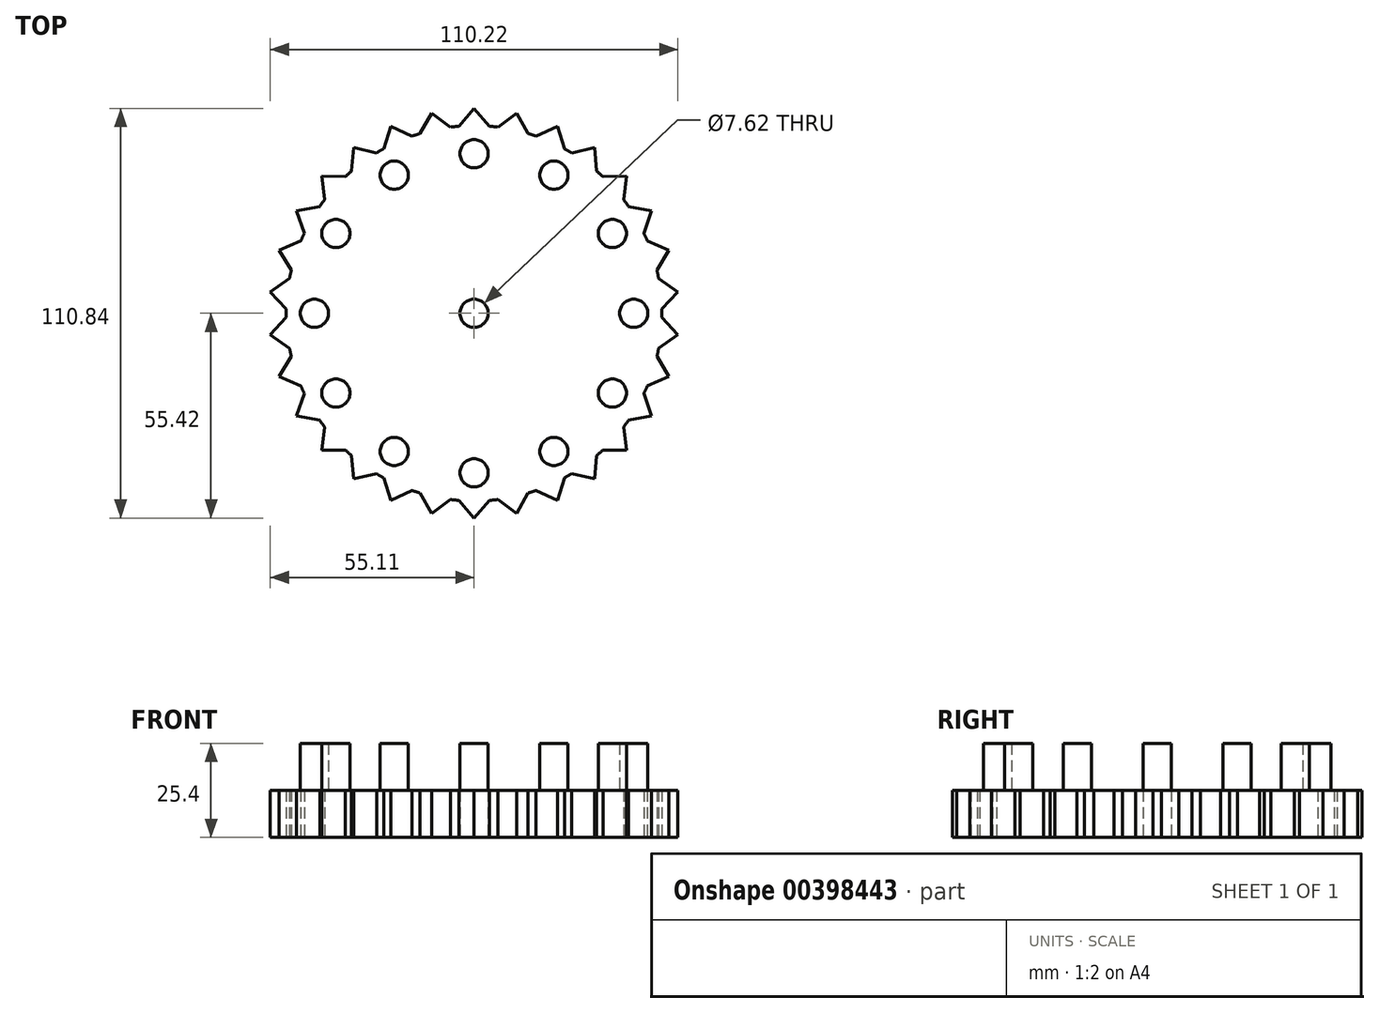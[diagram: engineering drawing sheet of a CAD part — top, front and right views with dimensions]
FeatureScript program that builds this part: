
annotation { "Feature Type Name" : "Feature", "Feature Type Description" : "" }
export const myFeature = defineFeature(function(context is Context, id is Id, definition is map)
    precondition{}
    {
        {
            var Q0;
            Q0=qCreatedBy(makeId("Top.planeOp"),FACE);
            var sketch = newSketch(context, id + "F0", { "sketchPlane" : qUnion([Q0])});
            skCircle(sketch, "E0", {"center": v(0, 0) * mm, "radius": 50.8 * mm});
            skCircle(sketch, "E1", {"center": v(0, 0) * mm, "radius": 3.81 * mm});
            skLineSegment(sketch, "E2", {"start": v(-4.17, 50.63) * mm, "end": v(0, 55.42) * mm});
            skLineSegment(sketch, "E3", {"start": v(0, 55.42) * mm, "end": v(4.17, 50.63) * mm});
            skLineSegment(sketch, "E4.1.0", {"start": v(-11.52, 54.2) * mm, "end": v(-6.45, 50.39) * mm});
            skLineSegment(sketch, "E4.1.1", {"start": v(-14.6, 48.65) * mm, "end": v(-11.52, 54.2) * mm});
            skLineSegment(sketch, "E4.2.0", {"start": v(-22.54, 50.62) * mm, "end": v(-16.78, 47.95) * mm});
            skLineSegment(sketch, "E4.2.1", {"start": v(-24.4, 44.55) * mm, "end": v(-22.54, 50.62) * mm});
            skLineSegment(sketch, "E4.3.0", {"start": v(-32.57, 44.83) * mm, "end": v(-26.38, 43.41) * mm});
            skLineSegment(sketch, "E4.3.1", {"start": v(-33.13, 38.5) * mm, "end": v(-32.57, 44.83) * mm});
            skLineSegment(sketch, "E4.4.0", {"start": v(-41.18, 37.08) * mm, "end": v(-34.83, 36.98) * mm});
            skLineSegment(sketch, "E4.4.1", {"start": v(-40.42, 30.78) * mm, "end": v(-41.18, 37.08) * mm});
            skLineSegment(sketch, "E4.5.0", {"start": v(-48, 27.7) * mm, "end": v(-41.76, 28.93) * mm});
            skLineSegment(sketch, "E4.5.1", {"start": v(-45.93, 21.7) * mm, "end": v(-48, 27.7) * mm});
            skLineSegment(sketch, "E4.6.0", {"start": v(-52.7, 17.12) * mm, "end": v(-46.86, 19.61) * mm});
            skLineSegment(sketch, "E4.6.1", {"start": v(-49.44, 11.68) * mm, "end": v(-52.7, 17.12) * mm});
            skLineSegment(sketch, "E4.7.0", {"start": v(-55.11, 5.8) * mm, "end": v(-49.91, 9.44) * mm});
            skLineSegment(sketch, "E4.7.1", {"start": v(-50.79, 1.14) * mm, "end": v(-55.11, 5.8) * mm});
            skLineSegment(sketch, "E4.8.0", {"start": v(-55.11, -5.8) * mm, "end": v(-50.79, -1.14) * mm});
            skLineSegment(sketch, "E4.8.1", {"start": v(-49.91, -9.44) * mm, "end": v(-55.11, -5.8) * mm});
            skLineSegment(sketch, "E4.9.0", {"start": v(-52.7, -17.12) * mm, "end": v(-49.44, -11.68) * mm});
            skLineSegment(sketch, "E4.9.1", {"start": v(-46.86, -19.61) * mm, "end": v(-52.7, -17.12) * mm});
            skLineSegment(sketch, "E4.10.0", {"start": v(-48, -27.7) * mm, "end": v(-45.93, -21.7) * mm});
            skLineSegment(sketch, "E4.10.1", {"start": v(-41.76, -28.93) * mm, "end": v(-48, -27.7) * mm});
            skLineSegment(sketch, "E4.11.0", {"start": v(-41.18, -37.08) * mm, "end": v(-40.42, -30.78) * mm});
            skLineSegment(sketch, "E4.11.1", {"start": v(-34.83, -36.98) * mm, "end": v(-41.18, -37.08) * mm});
            skLineSegment(sketch, "E4.12.0", {"start": v(-32.57, -44.83) * mm, "end": v(-33.13, -38.5) * mm});
            skLineSegment(sketch, "E4.12.1", {"start": v(-26.38, -43.41) * mm, "end": v(-32.57, -44.83) * mm});
            skLineSegment(sketch, "E4.13.0", {"start": v(-22.54, -50.62) * mm, "end": v(-24.4, -44.55) * mm});
            skLineSegment(sketch, "E4.13.1", {"start": v(-16.78, -47.95) * mm, "end": v(-22.54, -50.62) * mm});
            skLineSegment(sketch, "E4.14.0", {"start": v(-11.52, -54.2) * mm, "end": v(-14.6, -48.65) * mm});
            skLineSegment(sketch, "E4.14.1", {"start": v(-6.45, -50.39) * mm, "end": v(-11.52, -54.2) * mm});
            skLineSegment(sketch, "E4.15.0", {"start": v(0, -55.42) * mm, "end": v(-4.17, -50.63) * mm});
            skLineSegment(sketch, "E4.15.1", {"start": v(4.17, -50.63) * mm, "end": v(0, -55.42) * mm});
            skLineSegment(sketch, "E4.16.0", {"start": v(11.52, -54.2) * mm, "end": v(6.45, -50.39) * mm});
            skLineSegment(sketch, "E4.16.1", {"start": v(14.6, -48.65) * mm, "end": v(11.52, -54.2) * mm});
            skLineSegment(sketch, "E4.17.0", {"start": v(22.54, -50.62) * mm, "end": v(16.78, -47.95) * mm});
            skLineSegment(sketch, "E4.17.1", {"start": v(24.4, -44.55) * mm, "end": v(22.54, -50.62) * mm});
            skLineSegment(sketch, "E4.18.0", {"start": v(32.57, -44.83) * mm, "end": v(26.38, -43.41) * mm});
            skLineSegment(sketch, "E4.18.1", {"start": v(33.13, -38.5) * mm, "end": v(32.57, -44.83) * mm});
            skLineSegment(sketch, "E4.19.0", {"start": v(41.18, -37.08) * mm, "end": v(34.83, -36.98) * mm});
            skLineSegment(sketch, "E4.19.1", {"start": v(40.42, -30.78) * mm, "end": v(41.18, -37.08) * mm});
            skLineSegment(sketch, "E4.20.0", {"start": v(48, -27.7) * mm, "end": v(41.76, -28.93) * mm});
            skLineSegment(sketch, "E4.20.1", {"start": v(45.93, -21.7) * mm, "end": v(48, -27.7) * mm});
            skLineSegment(sketch, "E4.21.0", {"start": v(52.7, -17.12) * mm, "end": v(46.86, -19.61) * mm});
            skLineSegment(sketch, "E4.21.1", {"start": v(49.44, -11.68) * mm, "end": v(52.7, -17.12) * mm});
            skLineSegment(sketch, "E4.22.0", {"start": v(55.11, -5.8) * mm, "end": v(49.91, -9.44) * mm});
            skLineSegment(sketch, "E4.22.1", {"start": v(50.79, -1.14) * mm, "end": v(55.11, -5.8) * mm});
            skLineSegment(sketch, "E4.23.0", {"start": v(55.11, 5.8) * mm, "end": v(50.79, 1.14) * mm});
            skLineSegment(sketch, "E4.23.1", {"start": v(49.91, 9.44) * mm, "end": v(55.11, 5.8) * mm});
            skLineSegment(sketch, "E4.24.0", {"start": v(52.7, 17.12) * mm, "end": v(49.44, 11.68) * mm});
            skLineSegment(sketch, "E4.24.1", {"start": v(46.86, 19.61) * mm, "end": v(52.7, 17.12) * mm});
            skLineSegment(sketch, "E4.25.0", {"start": v(48, 27.7) * mm, "end": v(45.93, 21.7) * mm});
            skLineSegment(sketch, "E4.25.1", {"start": v(41.76, 28.93) * mm, "end": v(48, 27.7) * mm});
            skLineSegment(sketch, "E4.26.0", {"start": v(41.18, 37.08) * mm, "end": v(40.42, 30.78) * mm});
            skLineSegment(sketch, "E4.26.1", {"start": v(34.83, 36.98) * mm, "end": v(41.18, 37.08) * mm});
            skLineSegment(sketch, "E4.27.0", {"start": v(32.57, 44.83) * mm, "end": v(33.13, 38.5) * mm});
            skLineSegment(sketch, "E4.27.1", {"start": v(26.38, 43.41) * mm, "end": v(32.57, 44.83) * mm});
            skLineSegment(sketch, "E4.28.0", {"start": v(22.54, 50.62) * mm, "end": v(24.4, 44.55) * mm});
            skLineSegment(sketch, "E4.28.1", {"start": v(16.78, 47.95) * mm, "end": v(22.54, 50.62) * mm});
            skLineSegment(sketch, "E4.29.0", {"start": v(11.52, 54.2) * mm, "end": v(14.6, 48.65) * mm});
            skLineSegment(sketch, "E4.29.1", {"start": v(6.45, 50.39) * mm, "end": v(11.52, 54.2) * mm});
            skSolve(sketch);
        }
        {
            var Q0;
            Q0 = qSketchRegion(id + "F0", true);
            extrude(context, id + "F1", {"entities" : qUnion([Q0]), "depth" : 12.7 * mm});
        }
        {
            var Q0;
            Q0=makeQuery(id+"F1.opExtrude","CAP_FACE",FACE,{"disambiguationData":[OSD([sQuery(id+"F0.wireOp",EDGE,"E0"),sQuery(id+"F0.wireOp",EDGE,"E1")])],"isStart":false});
            var sketch = newSketch(context, id + "F2", { "sketchPlane" : qUnion([Q0])});
            skCircle(sketch, "E5", {"center": v(0, 43.18) * mm, "radius": 3.81 * mm});
            skCircle(sketch, "E6.1.0", {"center": v(-21.59, 37.4) * mm, "radius": 3.81 * mm});
            skCircle(sketch, "E6.2.0", {"center": v(-37.4, 21.6) * mm, "radius": 3.81 * mm});
            skCircle(sketch, "E6.3.0", {"center": v(-43.18, 0) * mm, "radius": 3.81 * mm});
            skCircle(sketch, "E6.4.0", {"center": v(-37.4, -21.59) * mm, "radius": 3.81 * mm});
            skCircle(sketch, "E6.5.0", {"center": v(-21.6, -37.4) * mm, "radius": 3.81 * mm});
            skCircle(sketch, "E6.6.0", {"center": v(0, -43.18) * mm, "radius": 3.81 * mm});
            skCircle(sketch, "E6.7.0", {"center": v(21.59, -37.4) * mm, "radius": 3.81 * mm});
            skCircle(sketch, "E6.8.0", {"center": v(37.4, -21.6) * mm, "radius": 3.81 * mm});
            skCircle(sketch, "E6.9.0", {"center": v(43.18, 0) * mm, "radius": 3.81 * mm});
            skCircle(sketch, "E6.10.0", {"center": v(37.4, 21.59) * mm, "radius": 3.81 * mm});
            skCircle(sketch, "E6.11.0", {"center": v(21.59, 37.4) * mm, "radius": 3.81 * mm});
            skPoint(sketch, "E6.center", {"position": v(0, 0) * mm});
            skLineSegment(sketch, "E7", {"start": v(0, 50.8) * mm, "end": v(0, 43.18) * mm});
            skSolve(sketch);
        }
        {
            var Q0;
            Q0=makeQuery(id+"F2.imprint","IMPRINT",FACE,{"disambiguationData":[TD([[makeQuery(id+"F2.imprint","IMPRINT",EDGE,{"derivedFrom":sQuery(id+"F2.wireOp",EDGE,"E6.5.0")}),1.0]])]});
            var Q1;
            Q1=makeQuery(id+"F2.imprint","IMPRINT",FACE,{"disambiguationData":[TD([[makeQuery(id+"F2.imprint","IMPRINT",EDGE,{"derivedFrom":sQuery(id+"F2.wireOp",EDGE,"E6.4.0")}),1.0]])]});
            var Q2;
            Q2=makeQuery(id+"F2.imprint","IMPRINT",FACE,{"disambiguationData":[TD([[makeQuery(id+"F2.imprint","IMPRINT",EDGE,{"derivedFrom":sQuery(id+"F2.wireOp",EDGE,"E6.3.0")}),1.0]])]});
            var Q3;
            Q3=makeQuery(id+"F2.imprint","IMPRINT",FACE,{"disambiguationData":[TD([[makeQuery(id+"F2.imprint","IMPRINT",EDGE,{"derivedFrom":sQuery(id+"F2.wireOp",EDGE,"E6.2.0")}),1.0]])]});
            var Q4;
            Q4=makeQuery(id+"F2.imprint","IMPRINT",FACE,{"disambiguationData":[TD([[makeQuery(id+"F2.imprint","IMPRINT",EDGE,{"derivedFrom":sQuery(id+"F2.wireOp",EDGE,"E6.1.0")}),1.0]])]});
            var Q5;
            Q5=makeQuery(id+"F2.imprint","IMPRINT",FACE,{"disambiguationData":[TD([[makeQuery(id+"F2.imprint","IMPRINT",EDGE,{"derivedFrom":sQuery(id+"F2.wireOp",EDGE,"E5")}),1.0]])]});
            var Q6;
            Q6=makeQuery(id+"F2.imprint","IMPRINT",FACE,{"disambiguationData":[TD([[makeQuery(id+"F2.imprint","IMPRINT",EDGE,{"derivedFrom":sQuery(id+"F2.wireOp",EDGE,"E6.11.0")}),1.0]])]});
            var Q7;
            Q7=makeQuery(id+"F2.imprint","IMPRINT",FACE,{"disambiguationData":[TD([[makeQuery(id+"F2.imprint","IMPRINT",EDGE,{"derivedFrom":sQuery(id+"F2.wireOp",EDGE,"E6.10.0")}),1.0]])]});
            var Q8;
            Q8=makeQuery(id+"F2.imprint","IMPRINT",FACE,{"disambiguationData":[TD([[makeQuery(id+"F2.imprint","IMPRINT",EDGE,{"derivedFrom":sQuery(id+"F2.wireOp",EDGE,"E6.9.0")}),1.0]])]});
            var Q9;
            Q9=makeQuery(id+"F2.imprint","IMPRINT",FACE,{"disambiguationData":[TD([[makeQuery(id+"F2.imprint","IMPRINT",EDGE,{"derivedFrom":sQuery(id+"F2.wireOp",EDGE,"E6.8.0")}),1.0]])]});
            var Q10;
            Q10=makeQuery(id+"F2.imprint","IMPRINT",FACE,{"disambiguationData":[TD([[makeQuery(id+"F2.imprint","IMPRINT",EDGE,{"derivedFrom":sQuery(id+"F2.wireOp",EDGE,"E6.7.0")}),1.0]])]});
            var Q11;
            Q11=makeQuery(id+"F2.imprint","IMPRINT",FACE,{"disambiguationData":[TD([[makeQuery(id+"F2.imprint","IMPRINT",EDGE,{"derivedFrom":sQuery(id+"F2.wireOp",EDGE,"E6.6.0")}),1.0]])]});
            extrude(context, id + "F3", {"entities" : qUnion([Q0, Q1, Q2, Q3, Q4, Q5, Q6, Q7, Q8, Q9, Q10, Q11]), "operationType" : NewBodyOperationType.ADD, "depth" : 12.7 * mm});
        }
    });
